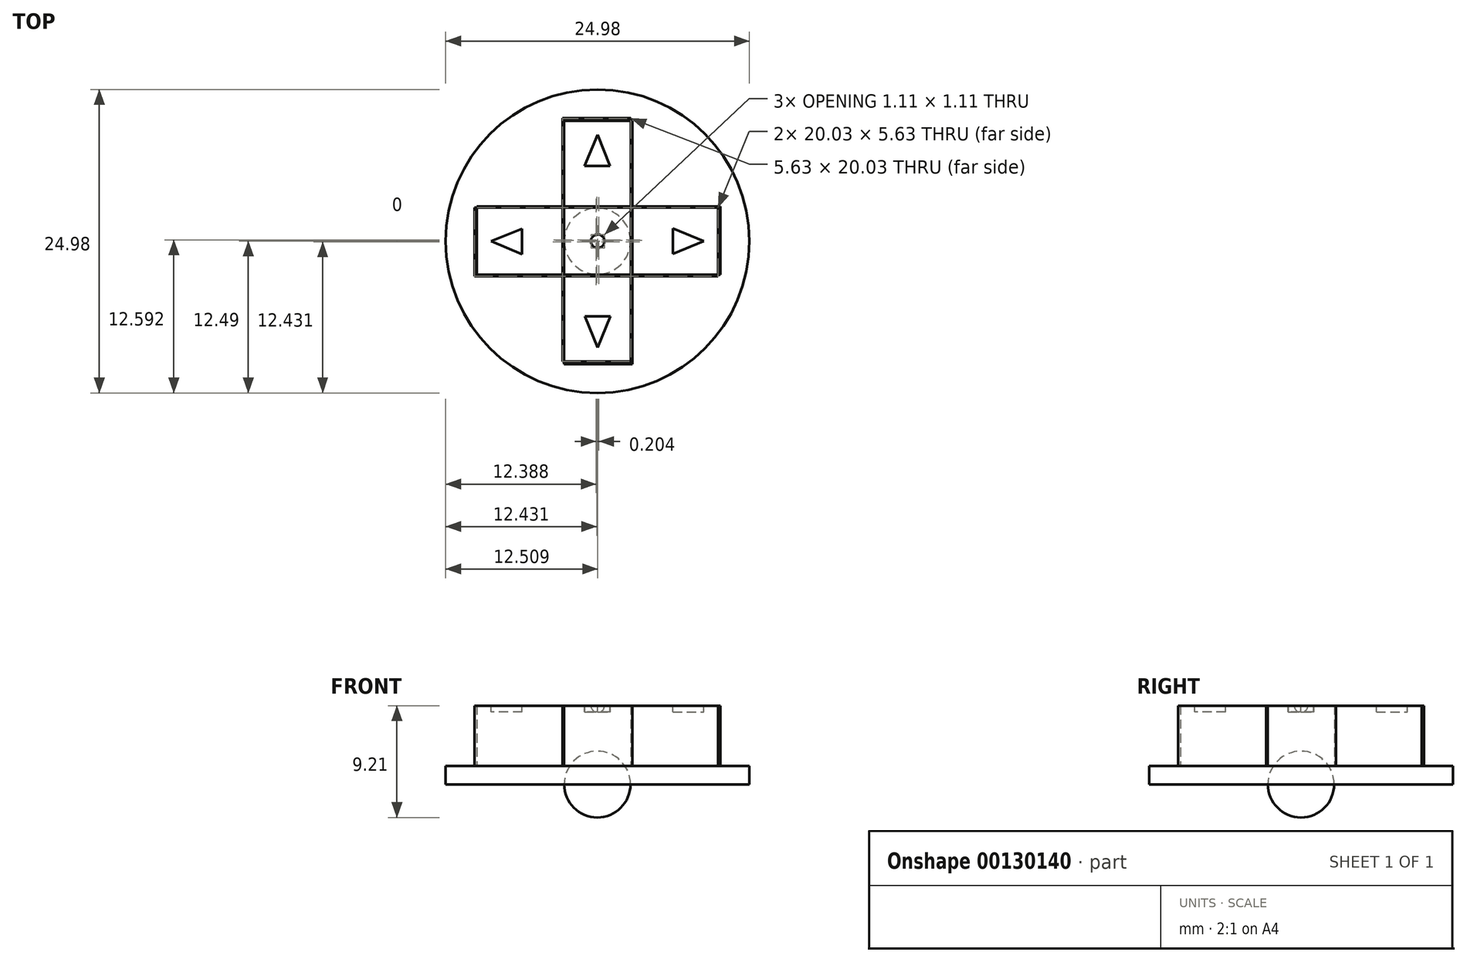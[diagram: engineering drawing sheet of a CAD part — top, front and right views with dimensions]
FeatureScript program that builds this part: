
annotation { "Feature Type Name" : "Feature", "Feature Type Description" : "" }
export const myFeature = defineFeature(function(context is Context, id is Id, definition is map)
    precondition{}
    {
        {
            var Q0;
            Q0=qCreatedBy(makeId("Top.planeOp"),FACE);
            var sketch = newSketch(context, id + "F0", { "sketchPlane" : qUnion([Q0])});
            skCircle(sketch, "E0", {"center": v(0, 0) * mm, "radius": 12.5 * mm});
            skSolve(sketch);
        }
        {
            var Q0;
            Q0 = qSketchRegion(id + "F0", true);
            extrude(context, id + "F1", {"entities" : qUnion([Q0]), "depth" : 1.5 * mm});
        }
        {
            var Q0;
            Q0=makeQuery(id+"F1.opExtrude","CAP_FACE",FACE,{"disambiguationData":[OSD([sQuery(id+"F0.wireOp",EDGE,"E0")])],"isStart":false});
            var sketch = newSketch(context, id + "F2", { "sketchPlane" : qUnion([Q0])});
            skLineSegment(sketch, "E1.bottom", {"start": v(-2.87, 10.12) * mm, "end": v(2.75, 10.12) * mm});
            skLineSegment(sketch, "E1.top", {"start": v(-2.87, -9.91) * mm, "end": v(2.75, -9.91) * mm});
            skLineSegment(sketch, "E1.left", {"start": v(-2.87, 10.12) * mm, "end": v(-2.87, -9.91) * mm});
            skLineSegment(sketch, "E1.right", {"start": v(2.75, 10.12) * mm, "end": v(2.75, -9.91) * mm});
            skSolve(sketch);
        }
        {
            var Q0;
            Q0 = qSketchRegion(id + "F2", true);
            extrude(context, id + "F3", {"entities" : qUnion([Q0]), "operationType" : NewBodyOperationType.ADD, "depth" : 4.98 * mm});
        }
        {
            var Q0;
            Q0=makeQuery(id+"F1.opExtrude","SWEPT_BODY",BODY,{"disambiguationData":[OSD([sQuery(id+"F0.wireOp",EDGE,"E0")])]});
            var Q1;
            Q1=makeQuery(id+"F1.opExtrude","CAP_EDGE",EDGE,{"disambiguationData":[OSD([sQuery(id+"F0.wireOp",EDGE,"E0")])],"isStart":false});
            transform(context, id + "F4", {"entities" : qUnion([Q0]), "transformType" : TransformType.ROTATION, "transformAxis" : qUnion([Q1]), "angle" : 90 * degree, "makeCopy" : true});
        }
        {
            var Q0;
            Q0=makeQuery(id+"F3.opExtrude","CAP_FACE",FACE,{"disambiguationData":[OSD([sQuery(id+"F2.wireOp",EDGE,"E1.bottom"),sQuery(id+"F2.wireOp",EDGE,"E1.top"),sQuery(id+"F2.wireOp",EDGE,"E1.left"),sQuery(id+"F2.wireOp",EDGE,"E1.right")])],"isStart":false});
            var sketch = newSketch(context, id + "F5", { "sketchPlane" : qUnion([Q0])});
            skLineSegment(sketch, "E2", {"start": v(0, 8.75) * mm, "end": v(-1.06, 6.2) * mm});
            skLineSegment(sketch, "E3", {"start": v(-1.06, 6.2) * mm, "end": v(1.03, 6.2) * mm});
            skLineSegment(sketch, "E4", {"start": v(1.03, 6.2) * mm, "end": v(0, 8.75) * mm});
            skSolve(sketch);
        }
        {
            var Q0;
            Q0 = qSketchRegion(id + "F5", true);
            extrude(context, id + "F6", {"entities" : qUnion([Q0]), "operationType" : NewBodyOperationType.REMOVE, "oppositeDirection" : true, "depth" : 0.5 * mm});
        }
        {
            var Q0;
            Q0=makeQuery(id+"F1.opExtrude","SWEPT_BODY",BODY,{"disambiguationData":[OSD([sQuery(id+"F0.wireOp",EDGE,"E0")])]});
            var Q1;
            Q1=makeQuery(id+"F1.opExtrude","CAP_EDGE",EDGE,{"disambiguationData":[OSD([sQuery(id+"F0.wireOp",EDGE,"E0")])],"isStart":false});
            transform(context, id + "F7", {"entities" : qUnion([Q0]), "transformType" : TransformType.ROTATION, "transformAxis" : qUnion([Q1]), "angle" : 90 * degree, "makeCopy" : true});
        }
        {
            var Q0;
            Q0=makeQuery(id+"F1.opExtrude","SWEPT_BODY",BODY,{"disambiguationData":[OSD([sQuery(id+"F0.wireOp",EDGE,"E0")])]});
            var Q1;
            Q1=makeQuery(id+"F4.opPattern","COPY",BODY,{"derivedFrom":makeQuery(id+"F1.opExtrude","SWEPT_BODY",BODY,{"disambiguationData":[OSD([sQuery(id+"F0.wireOp",EDGE,"E0")])]}),"instanceName":"1"});
            var Q2;
            Q2=makeQuery(id+"F1.opExtrude","CAP_EDGE",EDGE,{"disambiguationData":[OSD([sQuery(id+"F0.wireOp",EDGE,"E0")])],"isStart":false});
            transform(context, id + "F8", {"entities" : qUnion([Q0, Q1]), "transformType" : TransformType.ROTATION, "transformAxis" : qUnion([Q2]), "angle" : 180 * degree, "makeCopy" : true});
        }
        {
            var Q0;
            Q0=makeQuery(id+"F4.opPattern","COPY",BODY,{"derivedFrom":makeQuery(id+"F1.opExtrude","SWEPT_BODY",BODY,{"disambiguationData":[OSD([sQuery(id+"F0.wireOp",EDGE,"E0")])]}),"instanceName":"1"});
            var Q1;
            Q1=makeQuery(id+"F1.opExtrude","SWEPT_BODY",BODY,{"disambiguationData":[OSD([sQuery(id+"F0.wireOp",EDGE,"E0")])]});
            var Q2;
            Q2=makeQuery(id+"F1.opExtrude","CAP_EDGE",EDGE,{"disambiguationData":[OSD([sQuery(id+"F0.wireOp",EDGE,"E0")])],"isStart":false});
            transform(context, id + "F9", {"entities" : qUnion([Q0, Q1]), "transformType" : TransformType.ROTATION, "transformAxis" : qUnion([Q2]), "angle" : 270 * degree, "makeCopy" : true});
        }
        {
            var Q0;
            Q0=makeQuery(id+"F1.opExtrude","CAP_FACE",FACE,{"disambiguationData":[OSD([sQuery(id+"F0.wireOp",EDGE,"E0")])],"isStart":true});
            var sketch = newSketch(context, id + "F10", { "sketchPlane" : qUnion([Q0])});
            skPoint(sketch, "E5", {"position": v(0, 0) * mm});
            skArc(sketch, "E6", {"start": v(-2.74, 0) * mm, "mid": v(-0.01, -2.73) * mm, "end": v(2.71, 0) * mm});
            skLineSegment(sketch, "E7", {"start": v(-6.01, 0) * mm, "end": v(6.61, 0) * mm});
            skSolve(sketch);
        }
        {
            var Q0;
            Q0 = qSketchRegion(id + "F10", true);
            var Q1;
            Q1=sQuery(id+"F10.wireOp",EDGE,"E7");
            revolve(context, id + "F11", {"entities" : qUnion([Q0]), "axis" : qUnion([Q1]), "revolveType" : RevolveType.FULL});
        }
        {
            var Q0;
            Q0=makeQuery(id+"F3.opExtrude","CAP_FACE",FACE,{"disambiguationData":[OSD([sQuery(id+"F2.wireOp",EDGE,"E1.bottom"),sQuery(id+"F2.wireOp",EDGE,"E1.top"),sQuery(id+"F2.wireOp",EDGE,"E1.left"),sQuery(id+"F2.wireOp",EDGE,"E1.right")])],"isStart":false});
            var sketch = newSketch(context, id + "F12", { "sketchPlane" : qUnion([Q0])});
            skArc(sketch, "E8", {"start": v(0.58, 0) * mm, "mid": v(0.02, 0.56) * mm, "end": v(-0.54, 0) * mm});
            skLineSegment(sketch, "E9", {"start": v(-1.48, 0) * mm, "end": v(1.6, 0) * mm});
            skSolve(sketch);
        }
        {
            var Q0;
            {var subQ0=sQuery(id+"F12.wireOp",EDGE,"E8");Q0=makeQuery(id+"F12.imprint","IMPRINT",FACE,{"disambiguationData":[TD([[makeQuery(id+"F12.imprint","IMPRINT",EDGE,{"derivedFrom":subQ0}),1.0]])]});}
            var Q1;
            Q1=sQuery(id+"F12.wireOp",EDGE,"E9");
            revolve(context, id + "F13", {"operationType" : NewBodyOperationType.REMOVE, "entities" : qUnion([Q0]), "axis" : qUnion([Q1]), "revolveType" : RevolveType.FULL, "oppositeDirection" : true});
        }
    });
